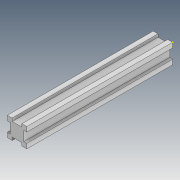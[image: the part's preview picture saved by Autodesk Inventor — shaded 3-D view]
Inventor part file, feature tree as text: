
AUTODESK INVENTOR PART (.ipt)
format: ipt  version: 2021 (Build 250183000, 183)  size: 128,512 bytes
history: native  units: mm
features: sketch x2, other x1, extrude x1
ambient origin geometry x8: Origin, YZ Plane, XZ Plane, XY Plane, X Axis, Y Axis, Z Axis, Center Point
bodies: Body1 (feature_tree)
feature tree (4):
  other  "Sólido1"
  extrude  "Extrusão1"  Depth=5.0mm
  sketch  "Esboço2"  dims[d6=3.0mm d7=10.0mm d8=3.0mm d9=5.0mm d10=5.0mm d11=3.0mm d12=10.0mm d13=5.0mm d14=5.0mm d15=3.0mm d16=10.0mm d17=3.0mm d18=5.0mm d19=3.0mm d20=10.0mm d21=150.0mm d22=0.0mm]
  sketch  "Esboço1"  dims[d4=5.0mm d5=5.0mm]
